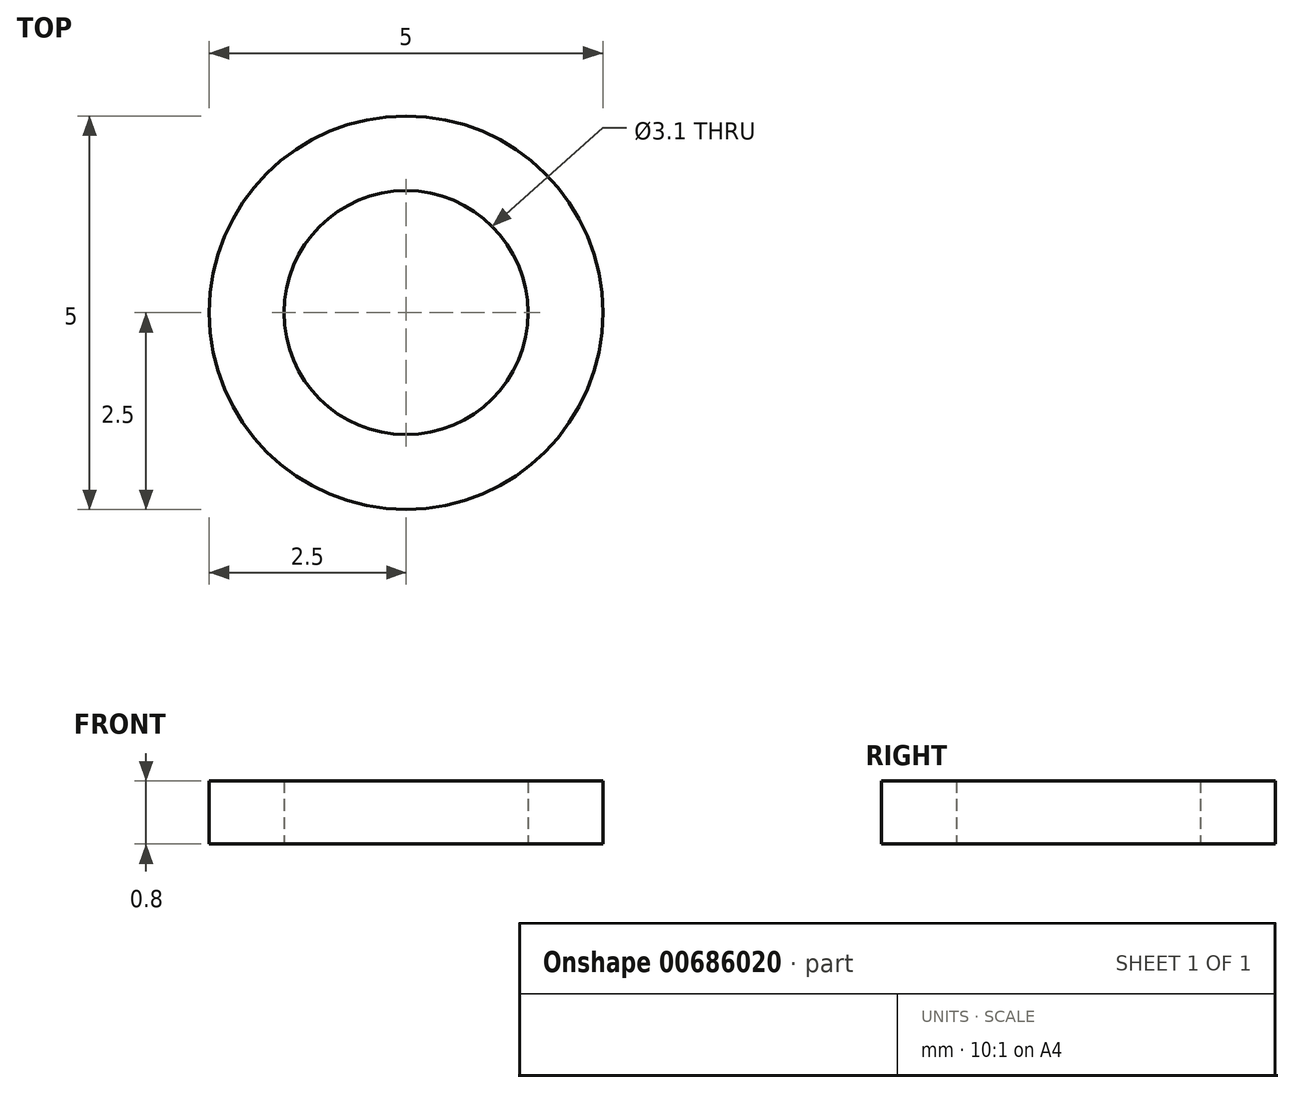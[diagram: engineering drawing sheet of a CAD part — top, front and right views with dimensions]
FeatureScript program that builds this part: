
annotation { "Feature Type Name" : "Feature", "Feature Type Description" : "" }
export const myFeature = defineFeature(function(context is Context, id is Id, definition is map)
    precondition{}
    {
        {
            var Q0;
            Q0=qCreatedBy(makeId("Top.planeOp"),FACE);
            var sketch = newSketch(context, id + "F0", { "sketchPlane" : qUnion([Q0])});
            skCircle(sketch, "E0", {"center": v(0, 0) * mm, "radius": 1.55 * mm});
            skCircle(sketch, "E1", {"center": v(0, 0) * mm, "radius": 2.5 * mm});
            skSolve(sketch);
        }
        {
            var Q0;
            Q0=makeQuery(id+"F0.imprint","IMPRINT",FACE,{"disambiguationData":[TD([[makeQuery(id+"F0.imprint","IMPRINT",EDGE,{"derivedFrom":sQuery(id+"F0.wireOp",EDGE,"E0")}),-1.0]])]});
            extrude(context, id + "F1", {"entities" : qUnion([Q0]), "depth" : .8 * mm, "offsetDistance" : 25 * mm});
        }
    });
